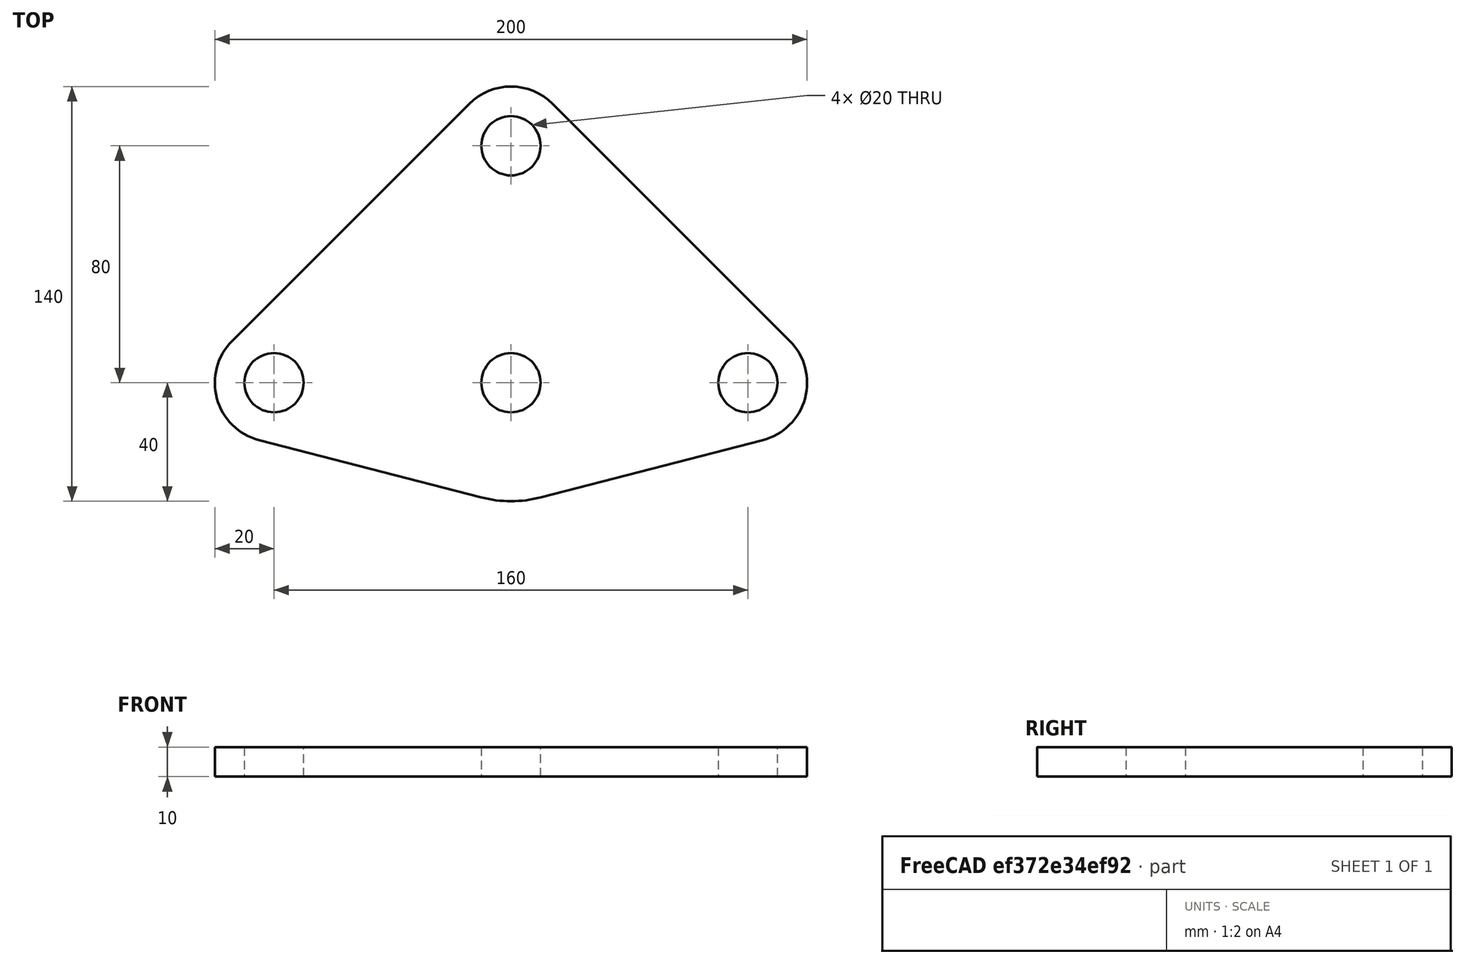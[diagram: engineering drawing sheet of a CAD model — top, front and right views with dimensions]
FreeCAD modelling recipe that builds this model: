
FCSTD DOCUMENT  (FreeCAD 0.20R29177 +426 (Git))
Label: rotary-2
License: All rights reserved
LicenseURL: http://en.wikipedia.org/wiki/All_rights_reserved
objects: Sketcher::SketchObject×1, PartDesign::Body×1, Part::Extrusion×1
note: 3 computed .brp shape members not serialized (recipe doc carries the construction recipe); baked Part::Feature solids carry a one-line shape summary decoded from their .brp

FEATURE [Sketcher::SketchObject] Sketch
  FullyConstrained = true
  MapMode = 5
  Support = -> [XY_Plane]
  sketch-geometry (16):
    g0: Circle CenterX=0 CenterY=0 CenterZ=0 NormalX=0 NormalY=0 NormalZ=1 AngleXU=0 Radius=100
    g1: ArcOfCircle CenterX=0 CenterY=0 CenterZ=0 NormalX=0 NormalY=0 NormalZ=1 AngleXU=0 Radius=40 StartAngle=4.45971 EndAngle=4.96507
    g2: LineSegment StartX=-80 StartY=0 StartZ=0 EndX=0 EndY=0 EndZ=0
    g3: LineSegment StartX=0 StartY=0 StartZ=0 EndX=80 EndY=0 EndZ=0
    g4: ArcOfCircle CenterX=-80 CenterY=0 CenterZ=0 NormalX=0 NormalY=0 NormalZ=1 AngleXU=0 Radius=20 StartAngle=2.35619 EndAngle=4.45971
    g5: ArcOfCircle CenterX=80 CenterY=0 CenterZ=0 NormalX=0 NormalY=0 NormalZ=1 AngleXU=0 Radius=20 StartAngle=4.96507 EndAngle=7.06858
    g6: LineSegment StartX=85 StartY=-19.3649 StartZ=0 EndX=10 EndY=-38.7298 EndZ=0
    g7: LineSegment StartX=-10 StartY=-38.7298 StartZ=0 EndX=-85 EndY=-19.3649 EndZ=0
    g8: Circle CenterX=0 CenterY=0 CenterZ=0 NormalX=0 NormalY=0 NormalZ=1 AngleXU=0 Radius=10
    g9: Circle CenterX=-80 CenterY=0 CenterZ=0 NormalX=0 NormalY=0 NormalZ=1 AngleXU=0 Radius=10
    g10: Circle CenterX=80 CenterY=0 CenterZ=0 NormalX=0 NormalY=0 NormalZ=1 AngleXU=0 Radius=10
    g11: LineSegment StartX=0 StartY=0 StartZ=0 EndX=0 EndY=80 EndZ=0
    g12: Circle CenterX=0 CenterY=80 CenterZ=0 NormalX=0 NormalY=0 NormalZ=1 AngleXU=0 Radius=10
    g13: ArcOfCircle CenterX=0 CenterY=80 CenterZ=0 NormalX=0 NormalY=0 NormalZ=1 AngleXU=0 Radius=20 StartAngle=0.785398 EndAngle=2.35619
    g14: LineSegment StartX=-94.1421 StartY=14.1421 StartZ=0 EndX=-14.1421 EndY=94.1421 EndZ=0
    g15: LineSegment StartX=14.1421 StartY=94.1421 StartZ=0 EndX=94.1421 EndY=14.1421 EndZ=0
  constraints (35):
    c: Coincident(g0,g-1)
    c: Diameter(g0) = 200
    c: Coincident(g1,g0)
    c: Diameter(g1) = 80
    c: PointOnObject(g2,g-1)
    c: Coincident(g2,g0)
    c: Coincident(g3,g0)
    c: PointOnObject(g3,g-1)
    c: Equal(g2,g3)
    c: DistanceX(g2,g3) = 160
    c: Coincident(g4,g2)
    c: Tangent(g4,g0)
    c: Coincident(g5,g3)
    c: Tangent(g5,g0)
    c: Tangent(g4,g7) = 1.5708
    c: Tangent(g5,g6) = 1.5708
    c: Coincident(g8,g0)
    c: Tangent(g1,g7) = 1.5708
    c: Tangent(g1,g6) = 1.5708
    c: Coincident(g9,g2)
    c: Equal(g9,g8)
    c: Diameter(g9) = 20
    c: Coincident(g10,g3)
    c: Equal(g10,g8)
    c: Coincident(g11,g1)
    c: PointOnObject(g11,g-2)
    c: Coincident(g12,g11)
    c: Diameter(g12) = 20
    c: Equal(g2,g11)
    c: Coincident(g13,g11)
    c: Tangent(g13,g0)
    c: Tangent(g13,g14) = 1.5708
    c: Tangent(g13,g15) = 1.5708
    c: Tangent(g14,g4) = 1.5708
    c: Tangent(g15,g5) = 1.5708
FEATURE [PartDesign::Body] Body
  Group = -> [Sketch]
  Origin = -> Origin
FEATURE [Part::Extrusion] Extrude
  Base = -> Sketch
  Dir = (0,0,1)
  DirMode = 2
  FaceMakerClass = Part::FaceMakerBullseye
  LengthFwd = 10
  LengthRev = 0
  Solid = true
  Symmetric = false
